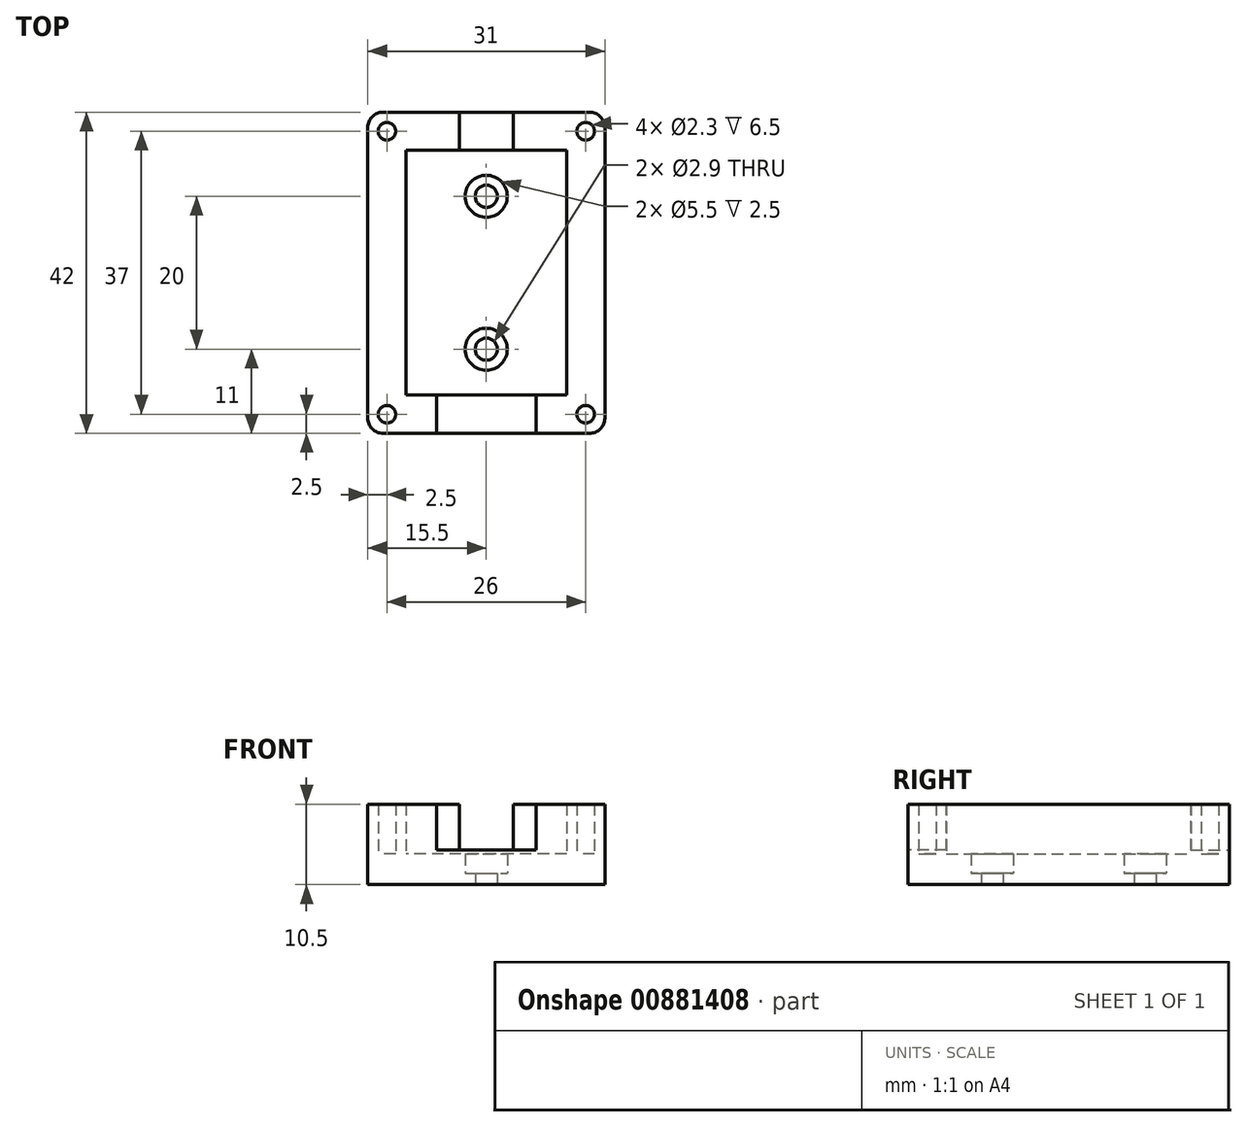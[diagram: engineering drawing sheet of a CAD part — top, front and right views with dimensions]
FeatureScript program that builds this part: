
annotation { "Feature Type Name" : "Feature", "Feature Type Description" : "" }
export const myFeature = defineFeature(function(context is Context, id is Id, definition is map)
    precondition{}
    {
        {
            var Q0;
            Q0=qCreatedBy(makeId("Top.planeOp"),FACE);
            var sketch = newSketch(context, id + "F0", { "sketchPlane" : qUnion([Q0])});
            skLineSegment(sketch, "E0.bottom", {"start": v(10.5, -16) * mm, "end": v(-10.5, -16) * mm});
            skLineSegment(sketch, "E0.top", {"start": v(10.5, 16) * mm, "end": v(-10.5, 16) * mm});
            skLineSegment(sketch, "E0.left", {"start": v(10.5, -16) * mm, "end": v(10.5, 16) * mm});
            skLineSegment(sketch, "E0.right", {"start": v(-10.5, -16) * mm, "end": v(-10.5, 16) * mm});
            skPoint(sketch, "E0.middle", {"position": v(0, 0) * mm});
            skLineSegment(sketch, "E1.0", {"start": v(15.5, 21) * mm, "end": v(-15.5, 21) * mm});
            skLineSegment(sketch, "E1.1", {"start": v(15.5, -21) * mm, "end": v(15.5, 21) * mm});
            skLineSegment(sketch, "E1.2", {"start": v(15.5, -21) * mm, "end": v(-15.5, -21) * mm});
            skLineSegment(sketch, "E1.3", {"start": v(-15.5, -21) * mm, "end": v(-15.5, 21) * mm});
            skPoint(sketch, "E2", {"position": v(13, 18.5) * mm});
            skPoint(sketch, "E3", {"position": v(-13, 18.5) * mm});
            skPoint(sketch, "E4", {"position": v(-13, -18.5) * mm});
            skPoint(sketch, "E5", {"position": v(13, -18.5) * mm});
            skCircle(sketch, "E6", {"center": v(-13, -18.5) * mm, "radius": 1.15 * mm});
            skCircle(sketch, "E7", {"center": v(13, -18.5) * mm, "radius": 1.15 * mm});
            skCircle(sketch, "E8", {"center": v(13, 18.5) * mm, "radius": 1.15 * mm});
            skCircle(sketch, "E9", {"center": v(-13, 18.5) * mm, "radius": 1.15 * mm});
            skSolve(sketch);
        }
        {
            var Q0;
            Q0=makeQuery(id+"F0.imprint","IMPRINT",FACE,{"disambiguationData":[TD([[makeQuery(id+"F0.imprint","IMPRINT",EDGE,{"derivedFrom":sQuery(id+"F0.wireOp",EDGE,"E0.bottom")}),1.0]])]});
            extrude(context, id + "F1", {"entities" : qUnion([Q0]), "depth" : 6.5 * mm, "offsetDistance" : 25 * mm});
        }
        {
            var Q0;
            Q0=makeQuery(id+"F1.opExtrude","CAP_FACE",FACE,{"disambiguationData":[OSD([sQuery(id+"F0.wireOp",EDGE,"E0.bottom"),sQuery(id+"F0.wireOp",EDGE,"E0.top"),sQuery(id+"F0.wireOp",EDGE,"E0.left"),sQuery(id+"F0.wireOp",EDGE,"E0.right"),sQuery(id+"F0.wireOp",EDGE,"E1.0"),sQuery(id+"F0.wireOp",EDGE,"E1.1"),sQuery(id+"F0.wireOp",EDGE,"E1.2"),sQuery(id+"F0.wireOp",EDGE,"E1.3"),sQuery(id+"F0.wireOp",EDGE,"E6"),sQuery(id+"F0.wireOp",EDGE,"E7"),sQuery(id+"F0.wireOp",EDGE,"E8"),sQuery(id+"F0.wireOp",EDGE,"E9")])],"isStart":true});
            var sketch = newSketch(context, id + "F2", { "sketchPlane" : qUnion([Q0])});
            skLineSegment(sketch, "E10.bottom", {"start": v(-15.5, 21) * mm, "end": v(15.5, 21) * mm});
            skLineSegment(sketch, "E10.top", {"start": v(-15.5, -21) * mm, "end": v(15.5, -21) * mm});
            skLineSegment(sketch, "E10.left", {"start": v(-15.5, 21) * mm, "end": v(-15.5, -21) * mm});
            skLineSegment(sketch, "E10.right", {"start": v(15.5, 21) * mm, "end": v(15.5, -21) * mm});
            skSolve(sketch);
        }
        {
            var Q0;
            Q0=makeQuery(id+"F2.imprint","IMPRINT",FACE,{"disambiguationData":[TD([[makeQuery(id+"F2.imprint","IMPRINT",EDGE,{"derivedFrom":sQuery(id+"F2.wireOp",EDGE,"E10.bottom")}),1.0]])]});
            var Q1;
            Q1=makeQuery(id+"F2.imprint","IMPRINT",FACE,{"disambiguationData":[TD([[makeQuery(id+"F2.imprint","IMPRINT",EDGE,{"derivedFrom":makeQuery(id+"F1.opExtrude","CAP_EDGE",EDGE,{"disambiguationData":[OSD([sQuery(id+"F0.wireOp",EDGE,"E0.bottom")])],"isStart":true})}),1.0]])]});
            var Q2;
            Q2=makeQuery(id+"F2.imprint","IMPRINT",FACE,{"disambiguationData":[TD([[makeQuery(id+"F2.imprint","IMPRINT",EDGE,{"derivedFrom":makeQuery(id+"F1.opExtrude","CAP_EDGE",EDGE,{"disambiguationData":[OSD([sQuery(id+"F0.wireOp",EDGE,"E7")])],"isStart":true})}),-1.0]])]});
            var Q3;
            Q3=makeQuery(id+"F2.imprint","IMPRINT",FACE,{"disambiguationData":[TD([[makeQuery(id+"F2.imprint","IMPRINT",EDGE,{"derivedFrom":makeQuery(id+"F1.opExtrude","CAP_EDGE",EDGE,{"disambiguationData":[OSD([sQuery(id+"F0.wireOp",EDGE,"E6")])],"isStart":true})}),-1.0]])]});
            var Q4;
            Q4=makeQuery(id+"F2.imprint","IMPRINT",FACE,{"disambiguationData":[TD([[makeQuery(id+"F2.imprint","IMPRINT",EDGE,{"derivedFrom":makeQuery(id+"F1.opExtrude","CAP_EDGE",EDGE,{"disambiguationData":[OSD([sQuery(id+"F0.wireOp",EDGE,"E9")])],"isStart":true})}),-1.0]])]});
            var Q5;
            Q5=makeQuery(id+"F2.imprint","IMPRINT",FACE,{"disambiguationData":[TD([[makeQuery(id+"F2.imprint","IMPRINT",EDGE,{"derivedFrom":makeQuery(id+"F1.opExtrude","CAP_EDGE",EDGE,{"disambiguationData":[OSD([sQuery(id+"F0.wireOp",EDGE,"E8")])],"isStart":true})}),-1.0]])]});
            extrude(context, id + "F3", {"entities" : qUnion([Q0, Q1, Q2, Q3, Q4, Q5]), "operationType" : NewBodyOperationType.ADD, "depth" : 4 * mm, "offsetDistance" : 25 * mm});
        }
        {
            var Q0;
            Q0=makeQuery(id+"F1.opExtrude","CAP_FACE",FACE,{"disambiguationData":[OSD([sQuery(id+"F0.wireOp",EDGE,"E0.bottom"),sQuery(id+"F0.wireOp",EDGE,"E0.top"),sQuery(id+"F0.wireOp",EDGE,"E0.left"),sQuery(id+"F0.wireOp",EDGE,"E0.right"),sQuery(id+"F0.wireOp",EDGE,"E1.0"),sQuery(id+"F0.wireOp",EDGE,"E1.1"),sQuery(id+"F0.wireOp",EDGE,"E1.2"),sQuery(id+"F0.wireOp",EDGE,"E1.3"),sQuery(id+"F0.wireOp",EDGE,"E6"),sQuery(id+"F0.wireOp",EDGE,"E7"),sQuery(id+"F0.wireOp",EDGE,"E8"),sQuery(id+"F0.wireOp",EDGE,"E9")])],"isStart":false});
            var sketch = newSketch(context, id + "F4", { "sketchPlane" : qUnion([Q0])});
            skPoint(sketch, "E11", {"position": v(6.5, -16) * mm});
            skPoint(sketch, "E12", {"position": v(6.5, -21) * mm});
            skPoint(sketch, "E13", {"position": v(-6.5, -16) * mm});
            skPoint(sketch, "E14", {"position": v(-6.5, -21) * mm});
            skLineSegment(sketch, "E15", {"start": v(-6.5, -16) * mm, "end": v(-6.5, -21) * mm});
            skLineSegment(sketch, "E16", {"start": v(6.5, -21) * mm, "end": v(6.5, -16) * mm});
            skPoint(sketch, "E17", {"position": v(3.5, 16) * mm});
            skPoint(sketch, "E18", {"position": v(-3.5, 16) * mm});
            skLineSegment(sketch, "E19", {"start": v(-3.5, 16) * mm, "end": v(-3.5, 21) * mm});
            skLineSegment(sketch, "E20", {"start": v(-3.5, 21) * mm, "end": v(3.5, 21) * mm});
            skLineSegment(sketch, "E21", {"start": v(3.5, 21) * mm, "end": v(3.5, 16) * mm});
            skSolve(sketch);
        }
        {
            var Q0;
            {var subQ0=sQuery(id+"F4.wireOp",EDGE,"E15");Q0=makeQuery(id+"F4.imprint","IMPRINT",FACE,{"disambiguationData":[TD([[makeQuery(id+"F4.imprint","IMPRINT",EDGE,{"derivedFrom":subQ0}),1.0]])]});}
            var Q1;
            {var subQ0=sQuery(id+"F4.wireOp",EDGE,"E19");Q1=makeQuery(id+"F4.imprint","IMPRINT",FACE,{"disambiguationData":[TD([[makeQuery(id+"F4.imprint","IMPRINT",EDGE,{"derivedFrom":subQ0}),-1.0]])]});}
            extrude(context, id + "F5", {"entities" : qUnion([Q0, Q1]), "operationType" : NewBodyOperationType.REMOVE, "oppositeDirection" : true, "depth" : 6 * mm, "offsetDistance" : 25 * mm});
        }
        {
            var Q0;
            Q0=makeQuery(id+"F3.boolean.opBoolean","MERGE",EDGE,{"derivedFrom":[makeQuery(id+"F1.opExtrude","SWEPT_EDGE",EDGE,{"disambiguationData":[OSD([sQuery(id+"F0.wireOp",EDGE,"E1.0"),sQuery(id+"F0.wireOp",EDGE,"E1.3")])]}),makeQuery(id+"F3.opExtrude","SWEPT_EDGE",EDGE,{"disambiguationData":[OSD([sQuery(id+"F2.wireOp",EDGE,"E10.top"),sQuery(id+"F2.wireOp",EDGE,"E10.left")])]})]});
            var Q1;
            Q1=makeQuery(id+"F3.boolean.opBoolean","MERGE",EDGE,{"derivedFrom":[makeQuery(id+"F1.opExtrude","SWEPT_EDGE",EDGE,{"disambiguationData":[OSD([sQuery(id+"F0.wireOp",EDGE,"E1.0"),sQuery(id+"F0.wireOp",EDGE,"E1.1")])]}),makeQuery(id+"F3.opExtrude","SWEPT_EDGE",EDGE,{"disambiguationData":[OSD([sQuery(id+"F2.wireOp",EDGE,"E10.top"),sQuery(id+"F2.wireOp",EDGE,"E10.right")])]})]});
            var Q2;
            Q2=makeQuery(id+"F3.boolean.opBoolean","MERGE",EDGE,{"derivedFrom":[makeQuery(id+"F1.opExtrude","SWEPT_EDGE",EDGE,{"disambiguationData":[OSD([sQuery(id+"F0.wireOp",EDGE,"E1.1"),sQuery(id+"F0.wireOp",EDGE,"E1.2")])]}),makeQuery(id+"F3.opExtrude","SWEPT_EDGE",EDGE,{"disambiguationData":[OSD([sQuery(id+"F2.wireOp",EDGE,"E10.bottom"),sQuery(id+"F2.wireOp",EDGE,"E10.right")])]})]});
            var Q3;
            Q3=makeQuery(id+"F3.boolean.opBoolean","MERGE",EDGE,{"derivedFrom":[makeQuery(id+"F1.opExtrude","SWEPT_EDGE",EDGE,{"disambiguationData":[OSD([sQuery(id+"F0.wireOp",EDGE,"E1.2"),sQuery(id+"F0.wireOp",EDGE,"E1.3")])]}),makeQuery(id+"F3.opExtrude","SWEPT_EDGE",EDGE,{"disambiguationData":[OSD([sQuery(id+"F2.wireOp",EDGE,"E10.bottom"),sQuery(id+"F2.wireOp",EDGE,"E10.left")])]})]});
            fillet(context, id + "F6", {"entities" : qUnion([Q0, Q1, Q2, Q3]), "tangentPropagation" : true, "radius" : 2 * mm, "defaultsChanged" : false, "vertexSettings" : [], "allowEdgeOverflow" : false});
        }
        {
            var Q0;
            Q0=makeQuery(id+"F3.boolean.opBoolean","SPLIT",FACE,{"disambiguationData":[TD([makeQuery(id+"F1.opExtrude","SWEPT_FACE",FACE,{"disambiguationData":[OSD([sQuery(id+"F0.wireOp",EDGE,"E0.bottom")])]})])],"derivedFrom":makeQuery(id+"F3.opExtrude","CAP_FACE",FACE,{"disambiguationData":[OSD([sQuery(id+"F2.wireOp",EDGE,"E10.bottom"),sQuery(id+"F2.wireOp",EDGE,"E10.top"),sQuery(id+"F2.wireOp",EDGE,"E10.left"),sQuery(id+"F2.wireOp",EDGE,"E10.right")])],"isStart":true})});
            var sketch = newSketch(context, id + "F7", { "sketchPlane" : qUnion([Q0])});
            skPoint(sketch, "E22", {"position": v(0, 10) * mm});
            skPoint(sketch, "E23", {"position": v(0, -10) * mm});
            skSolve(sketch);
        }
        {
            var Q0;
            Q0=sQuery(id+"F7.wireOp",VERTEX,"E22");
            var Q1;
            Q1=sQuery(id+"F7.wireOp",VERTEX,"E23");
            var Q2;
            Q2=makeQuery(id+"F1.opExtrude","SWEPT_BODY",BODY,{"disambiguationData":[OSD([sQuery(id+"F0.wireOp",EDGE,"E0.bottom"),sQuery(id+"F0.wireOp",EDGE,"E0.top"),sQuery(id+"F0.wireOp",EDGE,"E0.left"),sQuery(id+"F0.wireOp",EDGE,"E0.right"),sQuery(id+"F0.wireOp",EDGE,"E1.0"),sQuery(id+"F0.wireOp",EDGE,"E1.1"),sQuery(id+"F0.wireOp",EDGE,"E1.2"),sQuery(id+"F0.wireOp",EDGE,"E1.3"),sQuery(id+"F0.wireOp",EDGE,"E6"),sQuery(id+"F0.wireOp",EDGE,"E7"),sQuery(id+"F0.wireOp",EDGE,"E8"),sQuery(id+"F0.wireOp",EDGE,"E9")])]});
            hole(context, id + "F8", {"style" : HoleStyle.C_BORE, "endStyle" : HoleEndStyle.THROUGH, "standardTappedOrClearance" : lookupTablePath({ "fit" : "Normal", "standard" : "ISO", "size" : "M2.5", "type" : "Clearance" }), "standardBlindInLast" : lookupTablePath({ "fit" : "Normal", "standard" : "ISO", "engagement" : "75%", "pitch" : "0.35 mm", "size" : "M2.5", "type" : "Clearance & tapped" }), "holeDiameter" : 2.9 * mm, "cBoreDiameter" : 5.5 * mm, "cBoreDepth" : 2.5 * mm, "majorDiameter" : 5 * mm, "isTappedThrough" : true, "tappedDepth" : 12 * mm, "tapClearance" : 3, "locations" : qUnion([Q0, Q1]), "scope" : qUnion([Q2]), "startStyle" : HoleStartStyle.SKETCH});
        }
    });
